# Revit family: Haworth_Masters_ConvergentWorktop-Rectangular
name_source: partatom
category: Furniture Systems
revit_build: Autodesk Revit 2018 (Build: 20170223_1515(x64)
units: mm (PartAtom-declared; Revit-internal decimal feet)

## family parameters
Always vertical = Yes
Cut with Voids When Loaded = No
OmniClass Number = 23.40.70.14.64.21
OmniClass Title = Systems Furniture
Part Type = Normal
Room Calculation Point = No
Round Connector Dimension = Use Diameter
Shared = No
Work Plane-Based = No

## types (1)
- Haworth_Masters_ConvergentWorktop-Rectangular
    Actual Depth = 41"
    Actual Height = 30"
    Actual Support Depth = 38 1/2"
    Actual Width = 82"
    Assembly Code = E2020200
    Connector Block - Right = Yes
    Custom Size = No
    Depth = 42"
    Description = Masters Worksurface Rectangular - Height Adjustable
    Height = 30"
    Height Adjustable = Yes
    Hoop Leg = No
    Leg Finish = Haworth _ Paint _ Metallic Champagne
    Manufacturer = Haworth
    Max. Depth = 41"
    Max. Height = 47 11/16"
    Max. Width = 82"
    Min. Depth = 29"
    Min. Height = 28 11/16"
    Min. Width = 58"
    Min/Max Depth = 29, 35, 41 in.
    Min/Max Height = 28 11/16-32 11/16 in.
    Min/Max Width = 58-82 in. @ 6 in. Increments
    Model = Masters
    Revision Number = 1
    Size = Verify Final Dim. w/ Haworth
    Support Column = No
    Support Height = 28 13/16"
    Support Offset = 1 1/4"
    Sustainability Info = http://media.haworth.com
    URL = http://www.haworth.com
    URL - Product = http://www.haworth.com
    Warranty = http://www.haworth.com
    Width = 84"
    Worksurface Thickness = 1 3/16"

## geometry (parser evidence)
native form markers: Sweep x5
no freeform markers — native parametric forms only
